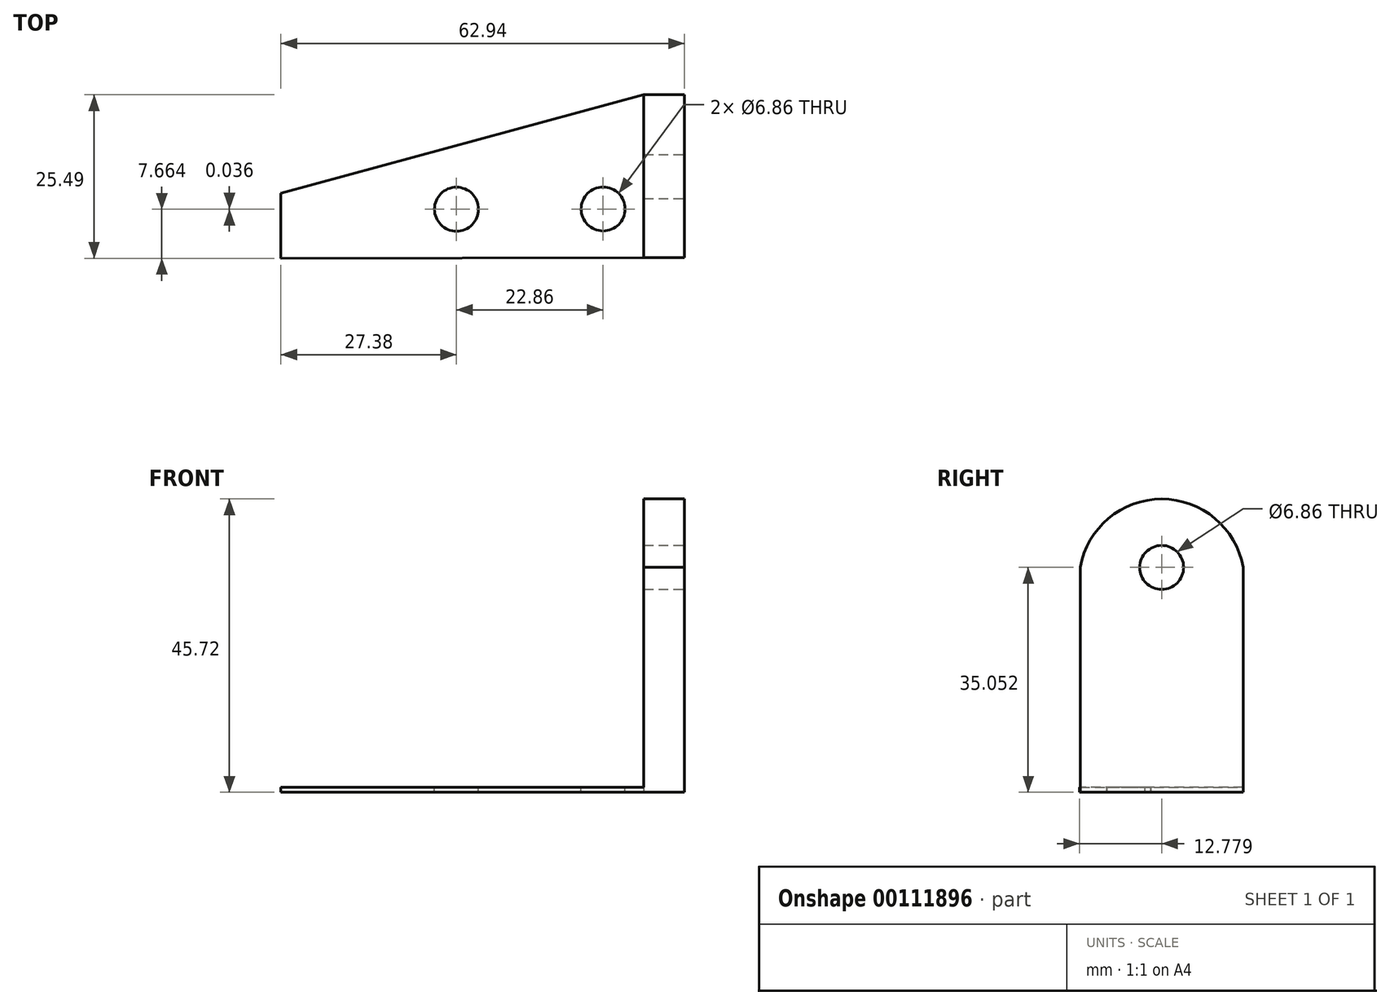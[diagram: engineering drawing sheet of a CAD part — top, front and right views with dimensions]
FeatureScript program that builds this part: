
annotation { "Feature Type Name" : "Feature", "Feature Type Description" : "" }
export const myFeature = defineFeature(function(context is Context, id is Id, definition is map)
    precondition{}
    {
        {
            var Q0;
            Q0=qCreatedBy(makeId("Top.planeOp"),FACE);
            var sketch = newSketch(context, id + "F0", { "sketchPlane" : qUnion([Q0])});
            skLineSegment(sketch, "E0.bottom", {"start": v(0, -17.4) * mm, "end": v(-6.35, -17.4) * mm});
            skLineSegment(sketch, "E0.top", {"start": v(0, 8) * mm, "end": v(-6.35, 8) * mm});
            skLineSegment(sketch, "E0.left", {"start": v(0, -17.4) * mm, "end": v(0, 8) * mm});
            skLineSegment(sketch, "E0.right", {"start": v(-6.35, -17.4) * mm, "end": v(-6.35, 8) * mm});
            skLineSegment(sketch, "E1", {"start": v(-6.35, 8) * mm, "end": v(-62.94, -7.32) * mm});
            skLineSegment(sketch, "E2", {"start": v(-62.94, -7.32) * mm, "end": v(-62.94, -17.48) * mm});
            skLineSegment(sketch, "E3", {"start": v(-62.94, -17.48) * mm, "end": v(-6.35, -17.4) * mm});
            skSolve(sketch);
        }
        {
            var Q0;
            Q0=makeQuery(id+"F0.imprint","IMPRINT",FACE,{"disambiguationData":[TD([[makeQuery(id+"F0.imprint","IMPRINT",EDGE,{"derivedFrom":sQuery(id+"F0.wireOp",EDGE,"E0.bottom")}),-1.0]])]});
            extrude(context, id + "F1", {"entities" : qUnion([Q0]), "depth" : 45.72 * mm});
        }
        {
            var Q0;
            Q0 = qSketchRegion(id + "F0", true);
            extrude(context, id + "F2", {"entities" : qUnion([Q0]), "operationType" : NewBodyOperationType.ADD, "depth" : 0.76 * mm});
        }
        {
            var Q0;
            Q0=makeQuery(id+"F1.opExtrude","SWEPT_FACE",FACE,{"disambiguationData":[OSD([sQuery(id+"F0.wireOp",EDGE,"E0.left")])]});
            var sketch = newSketch(context, id + "F3", { "sketchPlane" : qUnion([Q0])});
            skPoint(sketch, "E4", {"position": v(-4.7, 35.05) * mm});
            skArc(sketch, "E5", {"start": v(8, 35.05) * mm, "mid": v(-4.7, 45.72) * mm, "end": v(-17.4, 35.05) * mm});
            skCircle(sketch, "E6", {"center": v(-4.7, 35.05) * mm, "radius": 3.43 * mm});
            skSolve(sketch);
        }
        {
            var Q0;
            {var subQ0=sQuery(id+"F3.wireOp",EDGE,"E5");var subQ1=sQuery(id+"F0.wireOp",EDGE,"E0.left");var subQ4=makeQuery(id+"F1.opExtrude","CAP_EDGE",EDGE,{"disambiguationData":[OSD([subQ1])],"isStart":false});var subQ5=makeQuery(id+"F3.imprint","INTERSECT",VERTEX,{"derivedFrom":[subQ4,subQ0]});Q0=makeQuery(id+"F3.imprint","IMPRINT",FACE,{"disambiguationData":[TD([[makeQuery(id+"F3.imprint","IMPRINT",EDGE,{"disambiguationData":[TD([[subQ5,-1.0]])],"derivedFrom":subQ0}),-1.0]])]});}
            var Q1;
            {var subQ0=sQuery(id+"F3.wireOp",EDGE,"E5");var subQ1=sQuery(id+"F0.wireOp",EDGE,"E0.left");var subQ4=makeQuery(id+"F1.opExtrude","CAP_EDGE",EDGE,{"disambiguationData":[OSD([subQ1])],"isStart":false});var subQ5=makeQuery(id+"F3.imprint","INTERSECT",VERTEX,{"derivedFrom":[subQ4,subQ0]});Q1=makeQuery(id+"F3.imprint","IMPRINT",FACE,{"disambiguationData":[TD([[makeQuery(id+"F3.imprint","IMPRINT",EDGE,{"disambiguationData":[TD([[subQ5,1.0]])],"derivedFrom":subQ0}),-1.0]])]});}
            extrude(context, id + "F4", {"entities" : qUnion([Q0, Q1]), "operationType" : NewBodyOperationType.REMOVE, "oppositeDirection" : true, "depth" : 25.4 * mm});
        }
        {
            var Q0;
            Q0 = qSketchRegion(id + "F3", true);
            extrude(context, id + "F5", {"entities" : qUnion([Q0]), "operationType" : NewBodyOperationType.REMOVE, "oppositeDirection" : true, "depth" : 25.4 * mm});
        }
        {
            var Q0;
            Q0=makeQuery(id+"F2.opExtrude","CAP_FACE",FACE,{"disambiguationData":[OSD([sQuery(id+"F0.wireOp",EDGE,"E0.bottom"),sQuery(id+"F0.wireOp",EDGE,"E0.top"),sQuery(id+"F0.wireOp",EDGE,"E0.left"),sQuery(id+"F0.wireOp",EDGE,"E1"),sQuery(id+"F0.wireOp",EDGE,"E2"),sQuery(id+"F0.wireOp",EDGE,"E3")])],"isStart":false});
            var sketch = newSketch(context, id + "F6", { "sketchPlane" : qUnion([Q0])});
            skCircle(sketch, "E7", {"center": v(-12.7, -9.78) * mm, "radius": 3.43 * mm});
            skCircle(sketch, "E8", {"center": v(-35.56, -9.82) * mm, "radius": 3.43 * mm});
            skSolve(sketch);
        }
        {
            var Q0;
            Q0=makeQuery(id+"F6.imprint","IMPRINT",FACE,{"disambiguationData":[TD([[makeQuery(id+"F6.imprint","IMPRINT",EDGE,{"derivedFrom":sQuery(id+"F6.wireOp",EDGE,"E8")}),1.0]])]});
            var Q1;
            Q1=makeQuery(id+"F6.imprint","IMPRINT",FACE,{"disambiguationData":[TD([[makeQuery(id+"F6.imprint","IMPRINT",EDGE,{"derivedFrom":sQuery(id+"F6.wireOp",EDGE,"E7")}),1.0]])]});
            extrude(context, id + "F7", {"entities" : qUnion([Q0, Q1]), "operationType" : NewBodyOperationType.REMOVE, "oppositeDirection" : true, "depth" : 25.4 * mm});
        }
    });
